# Revit family: 357475xx0--Vitreous china wall - hung bidet - The Gap - Roca - 357475xx0
name_source: partatom
category: Plumbing Fixtures
units: mm (PartAtom-declared; Revit-internal decimal feet)

## family parameters
Always vertical = Yes
Cut with Voids When Loaded = No
Host = Wall
OmniClass Number = 23.45.00.00
OmniClass Title = Sanitary, Laundry, and Cleaning Equipment
Part Type = Normal
Room Calculation Point = No
Round Connector Dimension = Use Diameter
Shared = No

## types (2) — shared parameters
BIMobject category = Bidets
Date of publishing = 2015-03-06
Depth = 350.00
Description = Vitreous china wall-hung bidet
Design country = Spain
Eco green certification = No
Edition number = 2
Height = 315 mm  [stored 1.03346 ft]
IFC Classification = Sanitary Terminal
Installation type = Wall-hung
Length = 350 mm
Manufacturer URL = http://www.roca.com
Manufacturer country = Spain
Manufacturer name = Roca
Material main = Vitreous china
Model = 357475..0
NBS Reference Code = 35-06-11
NBS Reference Description = Bidets
Nominal height = 315.00
Nominal width = 540.00
Product SKU = 357475xx0
Product data url = http://roca.bimobject.com
Product family = The Gap
Product group = Bidets
QR code = https://www.roca.com
Suitable for Children = No
Suitable for Handicapped = No
Taphole diameter = 35 mm  [stored 0.114829 ft]
Technical description = http://www.roca.com
UNSPSC Code = 301815
URL = http://www.export.roca.com
Uniclass 1.4 Code = L7215
Uniclass 1.4 Description = Bidets
Uniclass 2.0 Code = PR-35-06-11
Uniclass 2.0 Description = Bidets
Weight Net (Kg) = 22.5
Width = 540 mm  [stored 1.77165 ft]

## type names (no varying parameters)
- Pergamon - The Gap - Roca
- White - The Gap - Roca

note: column(s) folded — value = type name in every type: Material

note: [stored X ft] marks values corroborated as IEEE doubles in the binary element streams (Revit-internal decimal feet)

## geometry (parser evidence)
native form markers: Blend x2, Sweep x2
no freeform markers — native parametric forms only
